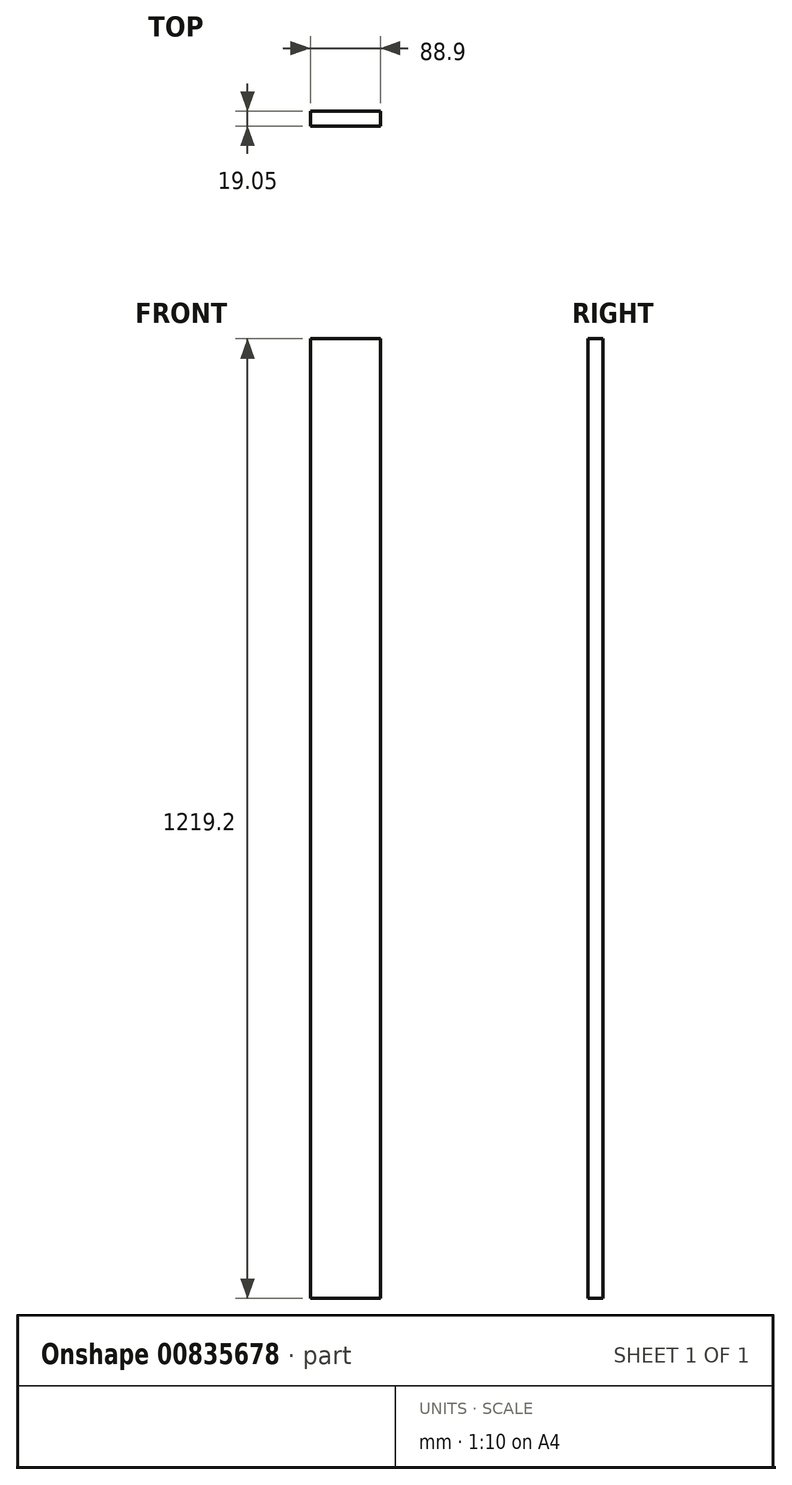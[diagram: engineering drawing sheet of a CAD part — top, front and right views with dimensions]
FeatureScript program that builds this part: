
annotation { "Feature Type Name" : "Feature", "Feature Type Description" : "" }
export const myFeature = defineFeature(function(context is Context, id is Id, definition is map)
    precondition{}
    {
        {
            var Q0;
            Q0=qCreatedBy(makeId("Front.planeOp"),FACE);
            var sketch = newSketch(context, id + "F0", { "sketchPlane" : qUnion([Q0])});
            skLineSegment(sketch, "E0.bottom", {"start": v(0, 0) * mm, "end": v(88.9, 0) * mm});
            skLineSegment(sketch, "E0.top", {"start": v(0, 1219.2) * mm, "end": v(88.9, 1219.2) * mm});
            skLineSegment(sketch, "E0.left", {"start": v(0, 0) * mm, "end": v(0, 1219.2) * mm});
            skLineSegment(sketch, "E0.right", {"start": v(88.9, 0) * mm, "end": v(88.9, 1219.2) * mm});
            skSolve(sketch);
        }
        {
            var Q0;
            Q0=qSketchRegion(id+"F0",true);
            extrude(context, id + "F1", {"entities" : qUnion([Q0]), "depth" : 19.05 * mm, "offsetDistance" : 25.4 * mm});
        }
    });
